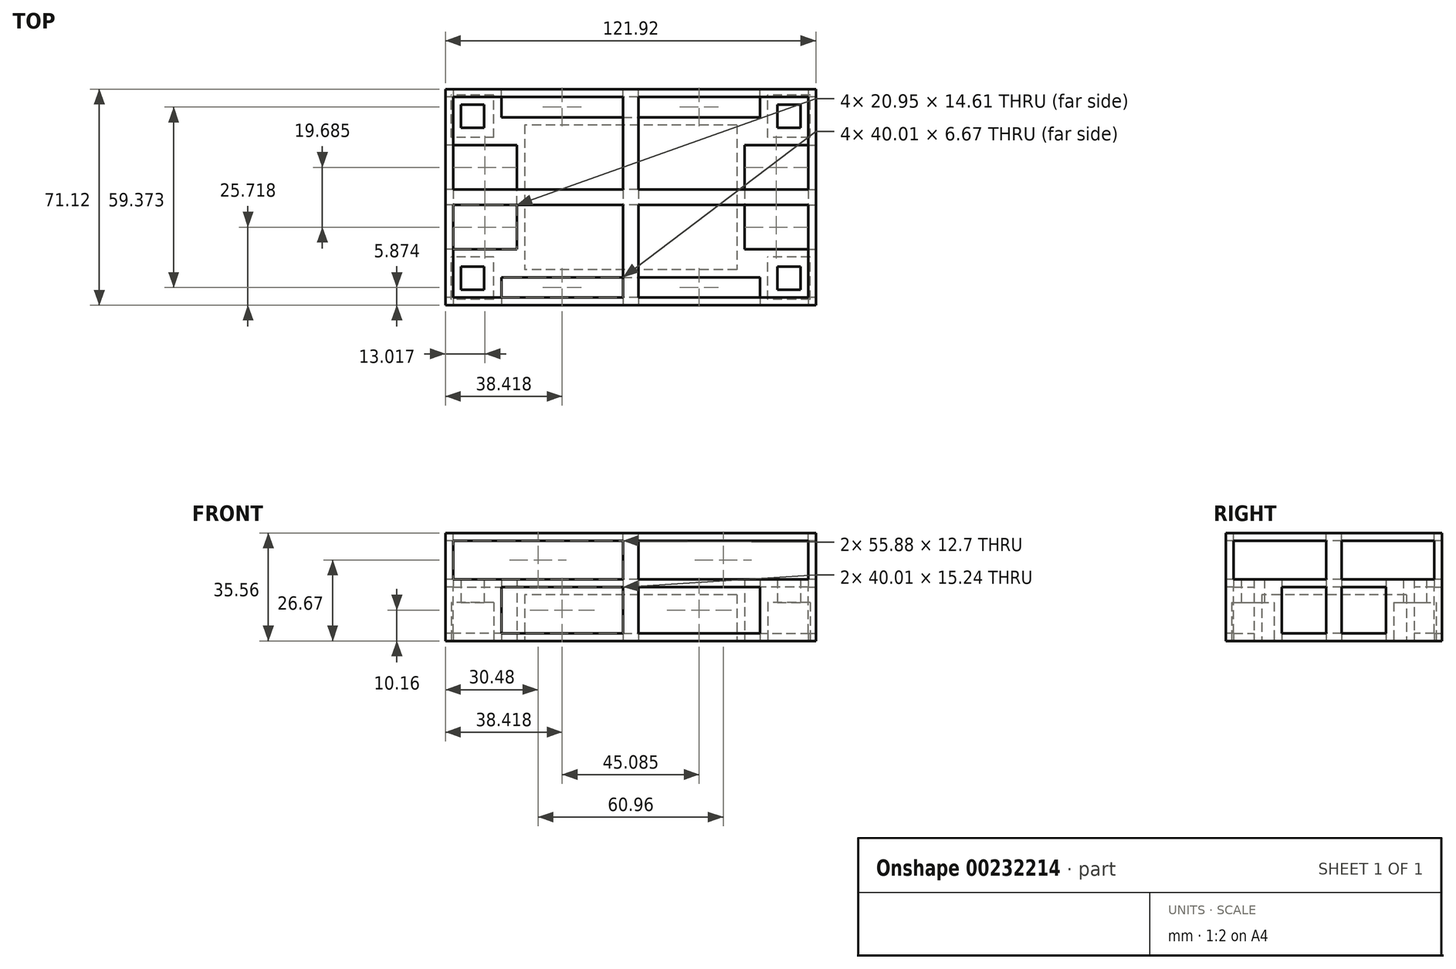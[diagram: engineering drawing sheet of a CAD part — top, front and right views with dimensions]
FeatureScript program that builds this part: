
annotation { "Feature Type Name" : "Feature", "Feature Type Description" : "" }
export const myFeature = defineFeature(function(context is Context, id is Id, definition is map)
    precondition{}
    {
        {
            var Q0;
            Q0=qCreatedBy(makeId("Top.planeOp"),FACE);
            var sketch = newSketch(context, id + "F0", { "sketchPlane" : qUnion([Q0])});
            skLineSegment(sketch, "E0.bottom", {"start": v(-60.96, 35.56) * mm, "end": v(60.96, 35.56) * mm});
            skLineSegment(sketch, "E0.top", {"start": v(-60.96, -35.56) * mm, "end": v(60.96, -35.56) * mm});
            skLineSegment(sketch, "E0.left", {"start": v(-60.96, 35.56) * mm, "end": v(-60.96, -35.56) * mm});
            skLineSegment(sketch, "E0.right", {"start": v(60.96, 35.56) * mm, "end": v(60.96, -35.56) * mm});
            skPoint(sketch, "E0.middle", {"position": v(0, 0) * mm});
            skSolve(sketch);
        }
        {
            var Q0;
            Q0=makeQuery(id+"F0.imprint","IMPRINT",FACE,{"disambiguationData":[TD([[makeQuery(id+"F0.imprint","IMPRINT",EDGE,{"derivedFrom":sQuery(id+"F0.wireOp",EDGE,"E0.bottom")}),-1.0]])]});
            extrude(context, id + "F1", {"entities" : qUnion([Q0]), "depth" : 35.56 * mm});
        }
        {
            var Q0;
            Q0=qCreatedBy(makeId("Top.planeOp"),FACE);
            var sketch = newSketch(context, id + "F2", { "sketchPlane" : qUnion([Q0])});
            skLineSegment(sketch, "E1.bottom", {"start": v(-52.07, 26.67) * mm, "end": v(52.07, 26.67) * mm});
            skLineSegment(sketch, "E1.top", {"start": v(-52.07, -26.67) * mm, "end": v(52.07, -26.67) * mm});
            skLineSegment(sketch, "E1.left", {"start": v(-52.07, 26.67) * mm, "end": v(-52.07, -26.67) * mm});
            skLineSegment(sketch, "E1.right", {"start": v(52.07, 26.67) * mm, "end": v(52.07, -26.67) * mm});
            skPoint(sketch, "E1.middle", {"position": v(0, 0) * mm});
            skLineSegment(sketch, "E2.bottom", {"start": v(-45.08, 19.68) * mm, "end": v(-59.05, 19.68) * mm});
            skLineSegment(sketch, "E2.top", {"start": v(-45.08, 33.66) * mm, "end": v(-59.05, 33.66) * mm});
            skLineSegment(sketch, "E2.left", {"start": v(-45.08, 19.68) * mm, "end": v(-45.08, 33.65) * mm});
            skLineSegment(sketch, "E2.right", {"start": v(-59.05, 19.68) * mm, "end": v(-59.05, 33.65) * mm});
            skPoint(sketch, "E2.middle", {"position": v(-52.07, 26.67) * mm});
            skLineSegment(sketch, "E3.bottom", {"start": v(-45.08, -33.65) * mm, "end": v(-59.05, -33.65) * mm});
            skLineSegment(sketch, "E3.top", {"start": v(-45.08, -19.68) * mm, "end": v(-59.05, -19.68) * mm});
            skLineSegment(sketch, "E3.left", {"start": v(-45.08, -33.65) * mm, "end": v(-45.08, -19.69) * mm});
            skLineSegment(sketch, "E3.right", {"start": v(-59.05, -33.65) * mm, "end": v(-59.05, -19.68) * mm});
            skPoint(sketch, "E3.middle", {"position": v(-52.07, -26.67) * mm});
            skLineSegment(sketch, "E4.bottom", {"start": v(59.05, -33.66) * mm, "end": v(45.08, -33.66) * mm});
            skLineSegment(sketch, "E4.top", {"start": v(59.05, -19.68) * mm, "end": v(45.08, -19.68) * mm});
            skLineSegment(sketch, "E4.left", {"start": v(59.05, -33.66) * mm, "end": v(59.05, -19.68) * mm});
            skLineSegment(sketch, "E4.right", {"start": v(45.08, -33.66) * mm, "end": v(45.08, -19.68) * mm});
            skPoint(sketch, "E4.middle", {"position": v(52.07, -26.67) * mm});
            skLineSegment(sketch, "E5.bottom", {"start": v(59.06, 19.69) * mm, "end": v(45.09, 19.69) * mm});
            skLineSegment(sketch, "E5.top", {"start": v(59.06, 33.66) * mm, "end": v(45.09, 33.66) * mm});
            skLineSegment(sketch, "E5.left", {"start": v(59.06, 19.69) * mm, "end": v(59.06, 33.66) * mm});
            skLineSegment(sketch, "E5.right", {"start": v(45.09, 19.69) * mm, "end": v(45.09, 33.66) * mm});
            skPoint(sketch, "E5.middle", {"position": v(52.07, 26.67) * mm});
            skLineSegment(sketch, "E6.bottom", {"start": v(-48.26, -22.86) * mm, "end": v(-55.88, -22.86) * mm});
            skLineSegment(sketch, "E6.top", {"start": v(-48.26, -30.48) * mm, "end": v(-55.88, -30.48) * mm});
            skLineSegment(sketch, "E6.left", {"start": v(-48.26, -22.86) * mm, "end": v(-48.26, -30.48) * mm});
            skLineSegment(sketch, "E6.right", {"start": v(-55.88, -22.86) * mm, "end": v(-55.88, -30.48) * mm});
            skLineSegment(sketch, "E7.bottom", {"start": v(-48.26, 30.48) * mm, "end": v(-55.88, 30.48) * mm});
            skLineSegment(sketch, "E7.top", {"start": v(-48.26, 22.86) * mm, "end": v(-55.88, 22.86) * mm});
            skLineSegment(sketch, "E7.left", {"start": v(-48.26, 30.48) * mm, "end": v(-48.26, 22.86) * mm});
            skLineSegment(sketch, "E7.right", {"start": v(-55.88, 30.48) * mm, "end": v(-55.88, 22.86) * mm});
            skLineSegment(sketch, "E8.bottom", {"start": v(55.88, -22.86) * mm, "end": v(48.26, -22.86) * mm});
            skLineSegment(sketch, "E8.top", {"start": v(55.88, -30.48) * mm, "end": v(48.26, -30.48) * mm});
            skLineSegment(sketch, "E8.left", {"start": v(55.88, -22.86) * mm, "end": v(55.88, -30.48) * mm});
            skLineSegment(sketch, "E8.right", {"start": v(48.26, -22.86) * mm, "end": v(48.26, -30.48) * mm});
            skLineSegment(sketch, "E9.bottom", {"start": v(55.88, 30.48) * mm, "end": v(48.26, 30.48) * mm});
            skLineSegment(sketch, "E9.top", {"start": v(55.88, 22.86) * mm, "end": v(48.26, 22.86) * mm});
            skLineSegment(sketch, "E9.left", {"start": v(55.88, 30.48) * mm, "end": v(55.88, 22.86) * mm});
            skLineSegment(sketch, "E9.right", {"start": v(48.26, 30.48) * mm, "end": v(48.26, 22.86) * mm});
            skSolve(sketch);
        }
        {
            var Q0;
            {var subQ4=sQuery(id+"F2.wireOp",EDGE,"E4.bottom");Q0=makeQuery(id+"F2.imprint","IMPRINT",FACE,{"disambiguationData":[TD([[makeQuery(id+"F2.imprint","IMPRINT",EDGE,{"derivedFrom":subQ4}),-1.0]])]});}
            var Q1;
            {var subQ0=sQuery(id+"F2.wireOp",EDGE,"E4.right");var subQ3=sQuery(id+"F2.wireOp",EDGE,"E1.top");var subQ4=makeQuery(id+"F2.imprint","INTERSECT",VERTEX,{"derivedFrom":[subQ3,subQ0]});Q1=makeQuery(id+"F2.imprint","IMPRINT",FACE,{"disambiguationData":[TD([[makeQuery(id+"F2.imprint","IMPRINT",EDGE,{"disambiguationData":[TD([[subQ4,-1.0]])],"derivedFrom":subQ3}),1.0]])]});}
            var Q2;
            {var subQ0=sQuery(id+"F2.wireOp",EDGE,"E1.right");var subQ1=sQuery(id+"F2.wireOp",EDGE,"E1.top");var subQ2=makeQuery(id+"F2.imprint","INTERSECT",VERTEX,{"derivedFrom":[subQ1,subQ0]});Q2=makeQuery(id+"F2.imprint","IMPRINT",FACE,{"disambiguationData":[TD([[makeQuery(id+"F2.imprint","IMPRINT",EDGE,{"disambiguationData":[TD([[subQ2,1.0]])],"derivedFrom":subQ1}),1.0]])]});}
            var Q3;
            {var subQ0=sQuery(id+"F2.wireOp",EDGE,"E8.top");Q3=makeQuery(id+"F2.imprint","IMPRINT",FACE,{"disambiguationData":[TD([[makeQuery(id+"F2.imprint","IMPRINT",EDGE,{"derivedFrom":subQ0}),-1.0]])]});}
            var Q4;
            {var subQ4=sQuery(id+"F2.wireOp",EDGE,"E5.top");Q4=makeQuery(id+"F2.imprint","IMPRINT",FACE,{"disambiguationData":[TD([[makeQuery(id+"F2.imprint","IMPRINT",EDGE,{"derivedFrom":subQ4}),1.0]])]});}
            var Q5;
            {var subQ0=sQuery(id+"F2.wireOp",EDGE,"E5.right");var subQ3=sQuery(id+"F2.wireOp",EDGE,"E1.bottom");var subQ4=makeQuery(id+"F2.imprint","INTERSECT",VERTEX,{"derivedFrom":[subQ3,subQ0]});Q5=makeQuery(id+"F2.imprint","IMPRINT",FACE,{"disambiguationData":[TD([[makeQuery(id+"F2.imprint","IMPRINT",EDGE,{"disambiguationData":[TD([[subQ4,-1.0]])],"derivedFrom":subQ3}),-1.0]])]});}
            var Q6;
            {var subQ4=sQuery(id+"F2.wireOp",EDGE,"E9.bottom");Q6=makeQuery(id+"F2.imprint","IMPRINT",FACE,{"disambiguationData":[TD([[makeQuery(id+"F2.imprint","IMPRINT",EDGE,{"derivedFrom":subQ4}),1.0]])]});}
            var Q7;
            {var subQ0=sQuery(id+"F2.wireOp",EDGE,"E1.right");var subQ1=sQuery(id+"F2.wireOp",EDGE,"E1.bottom");var subQ2=makeQuery(id+"F2.imprint","INTERSECT",VERTEX,{"derivedFrom":[subQ1,subQ0]});Q7=makeQuery(id+"F2.imprint","IMPRINT",FACE,{"disambiguationData":[TD([[makeQuery(id+"F2.imprint","IMPRINT",EDGE,{"disambiguationData":[TD([[subQ2,1.0]])],"derivedFrom":subQ1}),-1.0]])]});}
            var Q8;
            {var subQ0=sQuery(id+"F2.wireOp",EDGE,"E2.left");var subQ3=sQuery(id+"F2.wireOp",EDGE,"E1.bottom");var subQ4=makeQuery(id+"F2.imprint","INTERSECT",VERTEX,{"derivedFrom":[subQ3,subQ0]});Q8=makeQuery(id+"F2.imprint","IMPRINT",FACE,{"disambiguationData":[TD([[makeQuery(id+"F2.imprint","IMPRINT",EDGE,{"disambiguationData":[TD([[subQ4,1.0]])],"derivedFrom":subQ3}),-1.0]])]});}
            var Q9;
            {var subQ8=sQuery(id+"F2.wireOp",EDGE,"E7.bottom");Q9=makeQuery(id+"F2.imprint","IMPRINT",FACE,{"disambiguationData":[TD([[makeQuery(id+"F2.imprint","IMPRINT",EDGE,{"derivedFrom":subQ8}),1.0]])]});}
            var Q10;
            {var subQ0=sQuery(id+"F2.wireOp",EDGE,"E2.top");Q10=makeQuery(id+"F2.imprint","IMPRINT",FACE,{"disambiguationData":[TD([[makeQuery(id+"F2.imprint","IMPRINT",EDGE,{"derivedFrom":subQ0}),1.0]])]});}
            var Q11;
            {var subQ0=sQuery(id+"F2.wireOp",EDGE,"E1.left");var subQ1=sQuery(id+"F2.wireOp",EDGE,"E1.bottom");var subQ2=makeQuery(id+"F2.imprint","INTERSECT",VERTEX,{"derivedFrom":[subQ1,subQ0]});Q11=makeQuery(id+"F2.imprint","IMPRINT",FACE,{"disambiguationData":[TD([[makeQuery(id+"F2.imprint","IMPRINT",EDGE,{"disambiguationData":[TD([[subQ2,-1.0]])],"derivedFrom":subQ1}),-1.0]])]});}
            var Q12;
            {var subQ0=sQuery(id+"F2.wireOp",EDGE,"E3.bottom");Q12=makeQuery(id+"F2.imprint","IMPRINT",FACE,{"disambiguationData":[TD([[makeQuery(id+"F2.imprint","IMPRINT",EDGE,{"derivedFrom":subQ0}),-1.0]])]});}
            var Q13;
            {var subQ0=sQuery(id+"F2.wireOp",EDGE,"E6.top");Q13=makeQuery(id+"F2.imprint","IMPRINT",FACE,{"disambiguationData":[TD([[makeQuery(id+"F2.imprint","IMPRINT",EDGE,{"derivedFrom":subQ0}),-1.0]])]});}
            var Q14;
            {var subQ0=sQuery(id+"F2.wireOp",EDGE,"E1.left");var subQ1=sQuery(id+"F2.wireOp",EDGE,"E1.top");var subQ2=makeQuery(id+"F2.imprint","INTERSECT",VERTEX,{"derivedFrom":[subQ1,subQ0]});Q14=makeQuery(id+"F2.imprint","IMPRINT",FACE,{"disambiguationData":[TD([[makeQuery(id+"F2.imprint","IMPRINT",EDGE,{"disambiguationData":[TD([[subQ2,-1.0]])],"derivedFrom":subQ1}),1.0]])]});}
            var Q15;
            {var subQ0=sQuery(id+"F2.wireOp",EDGE,"E3.left");var subQ5=sQuery(id+"F2.wireOp",EDGE,"E1.top");var subQ6=makeQuery(id+"F2.imprint","INTERSECT",VERTEX,{"derivedFrom":[subQ5,subQ0]});Q15=makeQuery(id+"F2.imprint","IMPRINT",FACE,{"disambiguationData":[TD([[makeQuery(id+"F2.imprint","IMPRINT",EDGE,{"disambiguationData":[TD([[subQ6,1.0]])],"derivedFrom":subQ5}),1.0]])]});}
            extrude(context, id + "F3", {"entities" : qUnion([Q0, Q1, Q2, Q3, Q4, Q5, Q6, Q7, Q8, Q9, Q10, Q11, Q12, Q13, Q14, Q15]), "operationType" : NewBodyOperationType.REMOVE, "depth" : 12.7 * mm});
        }
        {
            var Q0;
            Q0=makeQuery(id+"F1.opExtrude","CAP_FACE",FACE,{"disambiguationData":[OSD([sQuery(id+"F0.wireOp",EDGE,"E0.bottom"),sQuery(id+"F0.wireOp",EDGE,"E0.top"),sQuery(id+"F0.wireOp",EDGE,"E0.left"),sQuery(id+"F0.wireOp",EDGE,"E0.right")])],"isStart":true});
            var sketch = newSketch(context, id + "F4", { "sketchPlane" : qUnion([Q0])});
            skLineSegment(sketch, "E10.bottom", {"start": v(34.93, -23.81) * mm, "end": v(-34.93, -23.81) * mm});
            skLineSegment(sketch, "E10.top", {"start": v(34.92, 23.81) * mm, "end": v(-34.93, 23.81) * mm});
            skLineSegment(sketch, "E10.left", {"start": v(34.93, -23.81) * mm, "end": v(34.92, 23.81) * mm});
            skLineSegment(sketch, "E10.right", {"start": v(-34.92, -23.81) * mm, "end": v(-34.93, 23.81) * mm});
            skPoint(sketch, "E10.middle", {"position": v(0, 0) * mm});
            skSolve(sketch);
        }
        {
            var Q0;
            Q0=makeQuery(id+"F4.imprint","IMPRINT",FACE,{"disambiguationData":[TD([[makeQuery(id+"F4.imprint","IMPRINT",EDGE,{"derivedFrom":sQuery(id+"F4.wireOp",EDGE,"E10.bottom")}),-1.0]])]});
            extrude(context, id + "F5", {"entities" : qUnion([Q0]), "operationType" : NewBodyOperationType.REMOVE, "oppositeDirection" : true, "depth" : 15.24 * mm});
        }
        {
            var Q0;
            Q0=makeQuery(id+"F1.opExtrude","SWEPT_FACE",FACE,{"disambiguationData":[OSD([sQuery(id+"F0.wireOp",EDGE,"E0.top")])]});
            var sketch = newSketch(context, id + "F6", { "sketchPlane" : qUnion([Q0])});
            skLineSegment(sketch, "E11", {"start": v(0, 0) * mm, "end": v(0, 35.56) * mm});
            skLineSegment(sketch, "E12.bottom", {"start": v(-60.96, 0) * mm, "end": v(60.96, 0) * mm});
            skLineSegment(sketch, "E12.top", {"start": v(-60.96, 17.78) * mm, "end": v(60.96, 17.78) * mm});
            skLineSegment(sketch, "E12.left", {"start": v(-60.96, 0) * mm, "end": v(-60.96, 17.78) * mm});
            skLineSegment(sketch, "E12.right", {"start": v(60.96, 0) * mm, "end": v(60.96, 17.78) * mm});
            skLineSegment(sketch, "E13.bottom", {"start": v(-60.96, 35.56) * mm, "end": v(60.96, 35.56) * mm});
            skLineSegment(sketch, "E13.left", {"start": v(-60.96, 35.56) * mm, "end": v(-60.96, 17.78) * mm});
            skLineSegment(sketch, "E13.right", {"start": v(60.96, 35.56) * mm, "end": v(60.96, 17.78) * mm});
            skLineSegment(sketch, "E14", {"start": v(-60.96, 35.56) * mm, "end": v(0, 35.56) * mm});
            skLineSegment(sketch, "E15", {"start": v(0, 35.56) * mm, "end": v(60.96, 35.56) * mm});
            skLineSegment(sketch, "E16", {"start": v(-30.48, 35.56) * mm, "end": v(-30.48, 17.78) * mm});
            skLineSegment(sketch, "E17", {"start": v(30.48, 35.56) * mm, "end": v(30.48, 17.78) * mm});
            skLineSegment(sketch, "E18", {"start": v(-60.96, 17.78) * mm, "end": v(-60.96, 35.56) * mm});
            skLineSegment(sketch, "E19", {"start": v(60.96, 17.78) * mm, "end": v(60.96, 35.56) * mm});
            skLineSegment(sketch, "E20", {"start": v(-60.96, 26.67) * mm, "end": v(0, 26.67) * mm});
            skLineSegment(sketch, "E21", {"start": v(0, 26.67) * mm, "end": v(60.96, 26.67) * mm});
            skLineSegment(sketch, "E22.bottom", {"start": v(-2.54, 33.02) * mm, "end": v(-58.42, 33.02) * mm});
            skLineSegment(sketch, "E22.top", {"start": v(-2.54, 20.32) * mm, "end": v(-58.42, 20.32) * mm});
            skLineSegment(sketch, "E22.left", {"start": v(-2.54, 33.02) * mm, "end": v(-2.54, 20.32) * mm});
            skLineSegment(sketch, "E22.right", {"start": v(-58.42, 33.02) * mm, "end": v(-58.42, 20.32) * mm});
            skPoint(sketch, "E22.middle", {"position": v(-30.48, 26.67) * mm});
            skLineSegment(sketch, "E23.bottom", {"start": v(58.42, 33.02) * mm, "end": v(2.54, 33.02) * mm});
            skLineSegment(sketch, "E23.top", {"start": v(58.42, 20.32) * mm, "end": v(2.54, 20.32) * mm});
            skLineSegment(sketch, "E23.left", {"start": v(58.42, 33.02) * mm, "end": v(58.42, 20.32) * mm});
            skLineSegment(sketch, "E23.right", {"start": v(2.54, 33.02) * mm, "end": v(2.54, 20.32) * mm});
            skPoint(sketch, "E23.middle", {"position": v(30.48, 26.67) * mm});
            skSolve(sketch);
        }
        {
            var Q0;
            {var subQ0=sQuery(id+"F6.wireOp",EDGE,"E22.bottom");var subQ1=sQuery(id+"F6.wireOp",EDGE,"E16");var subQ2=makeQuery(id+"F6.imprint","INTERSECT",VERTEX,{"derivedFrom":[subQ1,subQ0]});Q0=makeQuery(id+"F6.imprint","IMPRINT",FACE,{"disambiguationData":[TD([[makeQuery(id+"F6.imprint","IMPRINT",EDGE,{"disambiguationData":[TD([[subQ2,-1.0]])],"derivedFrom":subQ1}),-1.0]])]});}
            var Q1;
            {var subQ0=sQuery(id+"F6.wireOp",EDGE,"E22.bottom");var subQ1=sQuery(id+"F6.wireOp",EDGE,"E16");var subQ2=makeQuery(id+"F6.imprint","INTERSECT",VERTEX,{"derivedFrom":[subQ1,subQ0]});Q1=makeQuery(id+"F6.imprint","IMPRINT",FACE,{"disambiguationData":[TD([[makeQuery(id+"F6.imprint","IMPRINT",EDGE,{"disambiguationData":[TD([[subQ2,-1.0]])],"derivedFrom":subQ1}),1.0]])]});}
            var Q2;
            {var subQ0=sQuery(id+"F6.wireOp",EDGE,"E20");var subQ1=sQuery(id+"F6.wireOp",EDGE,"E16");var subQ2=makeQuery(id+"F6.imprint","INTERSECT",VERTEX,{"derivedFrom":[subQ1,subQ0]});Q2=makeQuery(id+"F6.imprint","IMPRINT",FACE,{"disambiguationData":[TD([[makeQuery(id+"F6.imprint","IMPRINT",EDGE,{"disambiguationData":[TD([[subQ2,-1.0]])],"derivedFrom":subQ1}),1.0]])]});}
            var Q3;
            {var subQ0=sQuery(id+"F6.wireOp",EDGE,"E20");var subQ1=sQuery(id+"F6.wireOp",EDGE,"E16");var subQ2=makeQuery(id+"F6.imprint","INTERSECT",VERTEX,{"derivedFrom":[subQ1,subQ0]});Q3=makeQuery(id+"F6.imprint","IMPRINT",FACE,{"disambiguationData":[TD([[makeQuery(id+"F6.imprint","IMPRINT",EDGE,{"disambiguationData":[TD([[subQ2,-1.0]])],"derivedFrom":subQ1}),-1.0]])]});}
            var Q4;
            {var subQ0=sQuery(id+"F6.wireOp",EDGE,"E23.bottom");var subQ1=sQuery(id+"F6.wireOp",EDGE,"E17");var subQ2=makeQuery(id+"F6.imprint","INTERSECT",VERTEX,{"derivedFrom":[subQ1,subQ0]});Q4=makeQuery(id+"F6.imprint","IMPRINT",FACE,{"disambiguationData":[TD([[makeQuery(id+"F6.imprint","IMPRINT",EDGE,{"disambiguationData":[TD([[subQ2,-1.0]])],"derivedFrom":subQ1}),-1.0]])]});}
            var Q5;
            {var subQ0=sQuery(id+"F6.wireOp",EDGE,"E21");var subQ1=sQuery(id+"F6.wireOp",EDGE,"E17");var subQ2=makeQuery(id+"F6.imprint","INTERSECT",VERTEX,{"derivedFrom":[subQ1,subQ0]});Q5=makeQuery(id+"F6.imprint","IMPRINT",FACE,{"disambiguationData":[TD([[makeQuery(id+"F6.imprint","IMPRINT",EDGE,{"disambiguationData":[TD([[subQ2,-1.0]])],"derivedFrom":subQ1}),-1.0]])]});}
            var Q6;
            {var subQ0=sQuery(id+"F6.wireOp",EDGE,"E23.bottom");var subQ1=sQuery(id+"F6.wireOp",EDGE,"E17");var subQ2=makeQuery(id+"F6.imprint","INTERSECT",VERTEX,{"derivedFrom":[subQ1,subQ0]});Q6=makeQuery(id+"F6.imprint","IMPRINT",FACE,{"disambiguationData":[TD([[makeQuery(id+"F6.imprint","IMPRINT",EDGE,{"disambiguationData":[TD([[subQ2,-1.0]])],"derivedFrom":subQ1}),1.0]])]});}
            var Q7;
            {var subQ0=sQuery(id+"F6.wireOp",EDGE,"E21");var subQ1=sQuery(id+"F6.wireOp",EDGE,"E17");var subQ2=makeQuery(id+"F6.imprint","INTERSECT",VERTEX,{"derivedFrom":[subQ1,subQ0]});Q7=makeQuery(id+"F6.imprint","IMPRINT",FACE,{"disambiguationData":[TD([[makeQuery(id+"F6.imprint","IMPRINT",EDGE,{"disambiguationData":[TD([[subQ2,-1.0]])],"derivedFrom":subQ1}),1.0]])]});}
            var Q8;
            Q8=makeQuery(id+"F1.opExtrude","SWEPT_FACE",FACE,{"disambiguationData":[OSD([sQuery(id+"F0.wireOp",EDGE,"E0.bottom")])]});
            extrude(context, id + "F7", {"entities" : qUnion([Q0, Q1, Q2, Q3, Q4, Q5, Q6, Q7]), "operationType" : NewBodyOperationType.REMOVE, "endBound" : BoundingType.UP_TO_SURFACE, "oppositeDirection" : true, "endBoundEntityFace" : qUnion([Q8]), "depth" : 25.4 * mm});
        }
        {
            var Q0;
            Q0=makeQuery(id+"F1.opExtrude","SWEPT_FACE",FACE,{"disambiguationData":[OSD([sQuery(id+"F0.wireOp",EDGE,"E0.left")])]});
            var sketch = newSketch(context, id + "F8", { "sketchPlane" : qUnion([Q0])});
            skLineSegment(sketch, "E24.bottom", {"start": v(-35.56, 0) * mm, "end": v(35.56, 0) * mm});
            skLineSegment(sketch, "E24.top", {"start": v(-35.56, 35.56) * mm, "end": v(35.56, 35.56) * mm});
            skLineSegment(sketch, "E24.left", {"start": v(-35.56, 0) * mm, "end": v(-35.56, 35.56) * mm});
            skLineSegment(sketch, "E24.right", {"start": v(35.56, 0) * mm, "end": v(35.56, 35.56) * mm});
            skLineSegment(sketch, "E25.top", {"start": v(-35.56, 17.78) * mm, "end": v(35.56, 17.78) * mm});
            skLineSegment(sketch, "E25.left", {"start": v(-35.56, 0) * mm, "end": v(-35.56, 17.78) * mm});
            skLineSegment(sketch, "E25.right", {"start": v(35.56, 0) * mm, "end": v(35.56, 17.78) * mm});
            skLineSegment(sketch, "E26.left", {"start": v(-35.56, 35.56) * mm, "end": v(-35.56, 17.78) * mm});
            skLineSegment(sketch, "E26.right", {"start": v(35.56, 35.56) * mm, "end": v(35.56, 17.78) * mm});
            skLineSegment(sketch, "E27", {"start": v(0, 0) * mm, "end": v(0, 35.56) * mm});
            skLineSegment(sketch, "E28", {"start": v(0, 35.56) * mm, "end": v(-35.56, 35.56) * mm});
            skLineSegment(sketch, "E29", {"start": v(-17.78, 35.56) * mm, "end": v(-17.78, 17.78) * mm});
            skLineSegment(sketch, "E30", {"start": v(-35.56, 26.67) * mm, "end": v(0, 26.67) * mm});
            skLineSegment(sketch, "E31", {"start": v(0, 26.67) * mm, "end": v(35.56, 26.67) * mm});
            skLineSegment(sketch, "E32", {"start": v(17.78, 35.56) * mm, "end": v(17.78, 17.78) * mm});
            skPoint(sketch, "E32.startSnap0", {"position": v(17.78, 26.67) * mm});
            skPoint(sketch, "E32.endSnap0", {"position": v(0, 17.78) * mm});
            skPoint(sketch, "E33", {"position": v(-17.78, 26.67) * mm});
            skLineSegment(sketch, "E34.bottom", {"start": v(-33.02, 33.02) * mm, "end": v(-2.54, 33.02) * mm});
            skLineSegment(sketch, "E34.top", {"start": v(-33.02, 20.32) * mm, "end": v(-2.54, 20.32) * mm});
            skLineSegment(sketch, "E34.left", {"start": v(-33.02, 33.02) * mm, "end": v(-33.02, 20.32) * mm});
            skLineSegment(sketch, "E34.right", {"start": v(-2.54, 33.02) * mm, "end": v(-2.54, 20.32) * mm});
            skLineSegment(sketch, "E35.bottom", {"start": v(2.54, 33.02) * mm, "end": v(33.02, 33.02) * mm});
            skLineSegment(sketch, "E35.top", {"start": v(2.54, 20.32) * mm, "end": v(33.02, 20.32) * mm});
            skLineSegment(sketch, "E35.left", {"start": v(2.54, 33.02) * mm, "end": v(2.54, 20.32) * mm});
            skLineSegment(sketch, "E35.right", {"start": v(33.02, 33.02) * mm, "end": v(33.02, 20.32) * mm});
            skSolve(sketch);
        }
        {
            var Q0;
            {var subQ0=sQuery(id+"F8.wireOp",EDGE,"E34.bottom");var subQ1=sQuery(id+"F8.wireOp",EDGE,"E29");var subQ2=makeQuery(id+"F8.imprint","INTERSECT",VERTEX,{"derivedFrom":[subQ1,subQ0]});Q0=makeQuery(id+"F8.imprint","IMPRINT",FACE,{"disambiguationData":[TD([[makeQuery(id+"F8.imprint","IMPRINT",EDGE,{"disambiguationData":[TD([[subQ2,-1.0]])],"derivedFrom":subQ1}),-1.0]])]});}
            var Q1;
            {var subQ0=sQuery(id+"F8.wireOp",EDGE,"E34.bottom");var subQ1=sQuery(id+"F8.wireOp",EDGE,"E29");var subQ2=makeQuery(id+"F8.imprint","INTERSECT",VERTEX,{"derivedFrom":[subQ1,subQ0]});Q1=makeQuery(id+"F8.imprint","IMPRINT",FACE,{"disambiguationData":[TD([[makeQuery(id+"F8.imprint","IMPRINT",EDGE,{"disambiguationData":[TD([[subQ2,-1.0]])],"derivedFrom":subQ1}),1.0]])]});}
            var Q2;
            {var subQ0=sQuery(id+"F8.wireOp",EDGE,"E30");var subQ1=sQuery(id+"F8.wireOp",EDGE,"E29");var subQ2=makeQuery(id+"F8.imprint","INTERSECT",VERTEX,{"derivedFrom":[subQ1,subQ0]});Q2=makeQuery(id+"F8.imprint","IMPRINT",FACE,{"disambiguationData":[TD([[makeQuery(id+"F8.imprint","IMPRINT",EDGE,{"disambiguationData":[TD([[subQ2,-1.0]])],"derivedFrom":subQ1}),1.0]])]});}
            var Q3;
            {var subQ0=sQuery(id+"F8.wireOp",EDGE,"E30");var subQ1=sQuery(id+"F8.wireOp",EDGE,"E29");var subQ2=makeQuery(id+"F8.imprint","INTERSECT",VERTEX,{"derivedFrom":[subQ1,subQ0]});Q3=makeQuery(id+"F8.imprint","IMPRINT",FACE,{"disambiguationData":[TD([[makeQuery(id+"F8.imprint","IMPRINT",EDGE,{"disambiguationData":[TD([[subQ2,-1.0]])],"derivedFrom":subQ1}),-1.0]])]});}
            var Q4;
            {var subQ0=sQuery(id+"F8.wireOp",EDGE,"E35.left");var subQ1=sQuery(id+"F8.wireOp",EDGE,"E31");var subQ2=makeQuery(id+"F8.imprint","INTERSECT",VERTEX,{"derivedFrom":[subQ1,subQ0]});Q4=makeQuery(id+"F8.imprint","IMPRINT",FACE,{"disambiguationData":[TD([[makeQuery(id+"F8.imprint","IMPRINT",EDGE,{"disambiguationData":[TD([[subQ2,-1.0]])],"derivedFrom":subQ1}),-1.0]])]});}
            var Q5;
            {var subQ0=sQuery(id+"F8.wireOp",EDGE,"E35.left");var subQ1=sQuery(id+"F8.wireOp",EDGE,"E31");var subQ2=makeQuery(id+"F8.imprint","INTERSECT",VERTEX,{"derivedFrom":[subQ1,subQ0]});Q5=makeQuery(id+"F8.imprint","IMPRINT",FACE,{"disambiguationData":[TD([[makeQuery(id+"F8.imprint","IMPRINT",EDGE,{"disambiguationData":[TD([[subQ2,-1.0]])],"derivedFrom":subQ1}),1.0]])]});}
            var Q6;
            {var subQ0=sQuery(id+"F8.wireOp",EDGE,"E32");var subQ1=sQuery(id+"F8.wireOp",EDGE,"E31");var subQ2=makeQuery(id+"F8.imprint","INTERSECT",VERTEX,{"derivedFrom":[subQ1,subQ0]});Q6=makeQuery(id+"F8.imprint","IMPRINT",FACE,{"disambiguationData":[TD([[makeQuery(id+"F8.imprint","IMPRINT",EDGE,{"disambiguationData":[TD([[subQ2,-1.0]])],"derivedFrom":subQ1}),1.0]])]});}
            var Q7;
            {var subQ0=sQuery(id+"F8.wireOp",EDGE,"E32");var subQ1=sQuery(id+"F8.wireOp",EDGE,"E31");var subQ2=makeQuery(id+"F8.imprint","INTERSECT",VERTEX,{"derivedFrom":[subQ1,subQ0]});Q7=makeQuery(id+"F8.imprint","IMPRINT",FACE,{"disambiguationData":[TD([[makeQuery(id+"F8.imprint","IMPRINT",EDGE,{"disambiguationData":[TD([[subQ2,-1.0]])],"derivedFrom":subQ1}),-1.0]])]});}
            var Q8;
            Q8=makeQuery(id+"F1.opExtrude","SWEPT_FACE",FACE,{"disambiguationData":[OSD([sQuery(id+"F0.wireOp",EDGE,"E0.right")])]});
            extrude(context, id + "F9", {"entities" : qUnion([Q0, Q1, Q2, Q3, Q4, Q5, Q6, Q7]), "operationType" : NewBodyOperationType.REMOVE, "endBound" : BoundingType.UP_TO_SURFACE, "oppositeDirection" : true, "endBoundEntityFace" : qUnion([Q8]), "depth" : 25.4 * mm});
        }
        {
            var Q0;
            Q0=makeQuery(id+"F1.opExtrude","CAP_FACE",FACE,{"disambiguationData":[OSD([sQuery(id+"F0.wireOp",EDGE,"E0.bottom"),sQuery(id+"F0.wireOp",EDGE,"E0.top"),sQuery(id+"F0.wireOp",EDGE,"E0.left"),sQuery(id+"F0.wireOp",EDGE,"E0.right")])],"isStart":false});
            var sketch = newSketch(context, id + "F10", { "sketchPlane" : qUnion([Q0])});
            skLineSegment(sketch, "E36.bottom", {"start": v(-60.96, 35.56) * mm, "end": v(60.96, 35.56) * mm});
            skLineSegment(sketch, "E36.top", {"start": v(-60.96, -35.56) * mm, "end": v(60.96, -35.56) * mm});
            skLineSegment(sketch, "E36.left", {"start": v(-60.96, 35.56) * mm, "end": v(-60.96, -35.56) * mm});
            skLineSegment(sketch, "E36.right", {"start": v(60.96, 35.56) * mm, "end": v(60.96, -35.56) * mm});
            skLineSegment(sketch, "E37.bottom", {"start": v(-60.96, 0) * mm, "end": v(0, 0) * mm});
            skLineSegment(sketch, "E37.top", {"start": v(-60.96, -35.56) * mm, "end": v(0, -35.56) * mm});
            skLineSegment(sketch, "E37.left", {"start": v(-60.96, 0) * mm, "end": v(-60.96, -35.56) * mm});
            skLineSegment(sketch, "E37.right", {"start": v(0, 0) * mm, "end": v(0, -35.56) * mm});
            skLineSegment(sketch, "E38.bottom", {"start": v(0, 0) * mm, "end": v(60.96, 0) * mm});
            skLineSegment(sketch, "E38.top", {"start": v(0, 35.56) * mm, "end": v(60.96, 35.56) * mm});
            skLineSegment(sketch, "E38.left", {"start": v(0, 0) * mm, "end": v(0, 35.56) * mm});
            skLineSegment(sketch, "E38.right", {"start": v(60.96, 0) * mm, "end": v(60.96, 35.56) * mm});
            skLineSegment(sketch, "E39.bottom", {"start": v(-60.96, 35.56) * mm, "end": v(0, 35.56) * mm});
            skLineSegment(sketch, "E39.left", {"start": v(-60.96, 35.56) * mm, "end": v(-60.96, 0) * mm});
            skLineSegment(sketch, "E39.right", {"start": v(0, 35.56) * mm, "end": v(0, 0) * mm});
            skLineSegment(sketch, "E40.top", {"start": v(0, -35.56) * mm, "end": v(60.96, -35.56) * mm});
            skLineSegment(sketch, "E40.right", {"start": v(60.96, 0) * mm, "end": v(60.96, -35.56) * mm});
            skLineSegment(sketch, "E41", {"start": v(-30.48, 0) * mm, "end": v(-30.48, 35.56) * mm});
            skLineSegment(sketch, "E42", {"start": v(-60.96, 17.78) * mm, "end": v(0, 17.78) * mm});
            skLineSegment(sketch, "E43", {"start": v(0, 17.78) * mm, "end": v(60.96, 17.78) * mm});
            skLineSegment(sketch, "E44", {"start": v(30.48, 35.56) * mm, "end": v(30.48, 0) * mm});
            skLineSegment(sketch, "E45", {"start": v(30.48, 0) * mm, "end": v(30.48, -35.56) * mm});
            skLineSegment(sketch, "E46", {"start": v(-30.48, -35.56) * mm, "end": v(-30.48, 0) * mm});
            skLineSegment(sketch, "E47", {"start": v(-60.96, -17.78) * mm, "end": v(0, -17.78) * mm});
            skLineSegment(sketch, "E48", {"start": v(0, -17.78) * mm, "end": v(60.96, -17.78) * mm});
            skPoint(sketch, "E49", {"position": v(-30.48, 17.78) * mm});
            skPoint(sketch, "E50", {"position": v(30.48, 17.78) * mm});
            skPoint(sketch, "E51", {"position": v(-30.48, -17.78) * mm});
            skPoint(sketch, "E52", {"position": v(30.48, -17.78) * mm});
            skLineSegment(sketch, "E53.bottom", {"start": v(-2.54, 33.02) * mm, "end": v(-58.42, 33.02) * mm});
            skLineSegment(sketch, "E53.top", {"start": v(-2.54, 2.54) * mm, "end": v(-58.42, 2.54) * mm});
            skLineSegment(sketch, "E53.left", {"start": v(-2.54, 33.02) * mm, "end": v(-2.54, 2.54) * mm});
            skLineSegment(sketch, "E53.right", {"start": v(-58.42, 33.02) * mm, "end": v(-58.42, 2.54) * mm});
            skLineSegment(sketch, "E54.bottom", {"start": v(58.42, 33.02) * mm, "end": v(2.54, 33.02) * mm});
            skLineSegment(sketch, "E54.top", {"start": v(58.42, 2.54) * mm, "end": v(2.54, 2.54) * mm});
            skLineSegment(sketch, "E54.left", {"start": v(58.42, 33.02) * mm, "end": v(58.42, 2.54) * mm});
            skLineSegment(sketch, "E54.right", {"start": v(2.54, 33.02) * mm, "end": v(2.54, 2.54) * mm});
            skLineSegment(sketch, "E55.bottom", {"start": v(-2.54, -2.54) * mm, "end": v(-58.42, -2.54) * mm});
            skLineSegment(sketch, "E55.top", {"start": v(-2.54, -33.02) * mm, "end": v(-58.42, -33.02) * mm});
            skLineSegment(sketch, "E55.left", {"start": v(-2.54, -2.54) * mm, "end": v(-2.54, -33.02) * mm});
            skLineSegment(sketch, "E55.right", {"start": v(-58.42, -2.54) * mm, "end": v(-58.42, -33.02) * mm});
            skLineSegment(sketch, "E56.bottom", {"start": v(58.42, -33.02) * mm, "end": v(2.54, -33.02) * mm});
            skLineSegment(sketch, "E56.top", {"start": v(58.42, -2.54) * mm, "end": v(2.54, -2.54) * mm});
            skLineSegment(sketch, "E56.left", {"start": v(58.42, -33.02) * mm, "end": v(58.42, -2.54) * mm});
            skLineSegment(sketch, "E56.right", {"start": v(2.54, -33.02) * mm, "end": v(2.54, -2.54) * mm});
            skSolve(sketch);
        }
        {
            var Q0;
            {var subQ0=sQuery(id+"F10.wireOp",EDGE,"E42");var subQ1=sQuery(id+"F10.wireOp",EDGE,"E41");var subQ2=makeQuery(id+"F10.imprint","INTERSECT",VERTEX,{"derivedFrom":[subQ1,subQ0]});Q0=makeQuery(id+"F10.imprint","IMPRINT",FACE,{"disambiguationData":[TD([[makeQuery(id+"F10.imprint","IMPRINT",EDGE,{"disambiguationData":[TD([[subQ2,-1.0]])],"derivedFrom":subQ1}),1.0]])]});}
            var Q1;
            {var subQ0=sQuery(id+"F10.wireOp",EDGE,"E42");var subQ1=sQuery(id+"F10.wireOp",EDGE,"E41");var subQ2=makeQuery(id+"F10.imprint","INTERSECT",VERTEX,{"derivedFrom":[subQ1,subQ0]});Q1=makeQuery(id+"F10.imprint","IMPRINT",FACE,{"disambiguationData":[TD([[makeQuery(id+"F10.imprint","IMPRINT",EDGE,{"disambiguationData":[TD([[subQ2,-1.0]])],"derivedFrom":subQ1}),-1.0]])]});}
            var Q2;
            {var subQ0=sQuery(id+"F10.wireOp",EDGE,"E53.top");var subQ1=sQuery(id+"F10.wireOp",EDGE,"E41");var subQ2=makeQuery(id+"F10.imprint","INTERSECT",VERTEX,{"derivedFrom":[subQ1,subQ0]});Q2=makeQuery(id+"F10.imprint","IMPRINT",FACE,{"disambiguationData":[TD([[makeQuery(id+"F10.imprint","IMPRINT",EDGE,{"disambiguationData":[TD([[subQ2,-1.0]])],"derivedFrom":subQ1}),-1.0]])]});}
            var Q3;
            {var subQ0=sQuery(id+"F10.wireOp",EDGE,"E53.top");var subQ1=sQuery(id+"F10.wireOp",EDGE,"E41");var subQ2=makeQuery(id+"F10.imprint","INTERSECT",VERTEX,{"derivedFrom":[subQ1,subQ0]});Q3=makeQuery(id+"F10.imprint","IMPRINT",FACE,{"disambiguationData":[TD([[makeQuery(id+"F10.imprint","IMPRINT",EDGE,{"disambiguationData":[TD([[subQ2,-1.0]])],"derivedFrom":subQ1}),1.0]])]});}
            var Q4;
            {var subQ0=sQuery(id+"F10.wireOp",EDGE,"E54.right");var subQ1=sQuery(id+"F10.wireOp",EDGE,"E43");var subQ2=makeQuery(id+"F10.imprint","INTERSECT",VERTEX,{"derivedFrom":[subQ1,subQ0]});Q4=makeQuery(id+"F10.imprint","IMPRINT",FACE,{"disambiguationData":[TD([[makeQuery(id+"F10.imprint","IMPRINT",EDGE,{"disambiguationData":[TD([[subQ2,-1.0]])],"derivedFrom":subQ1}),1.0]])]});}
            var Q5;
            {var subQ0=sQuery(id+"F10.wireOp",EDGE,"E54.right");var subQ1=sQuery(id+"F10.wireOp",EDGE,"E43");var subQ2=makeQuery(id+"F10.imprint","INTERSECT",VERTEX,{"derivedFrom":[subQ1,subQ0]});Q5=makeQuery(id+"F10.imprint","IMPRINT",FACE,{"disambiguationData":[TD([[makeQuery(id+"F10.imprint","IMPRINT",EDGE,{"disambiguationData":[TD([[subQ2,-1.0]])],"derivedFrom":subQ1}),-1.0]])]});}
            var Q6;
            {var subQ0=sQuery(id+"F10.wireOp",EDGE,"E44");var subQ1=sQuery(id+"F10.wireOp",EDGE,"E43");var subQ2=makeQuery(id+"F10.imprint","INTERSECT",VERTEX,{"derivedFrom":[subQ1,subQ0]});Q6=makeQuery(id+"F10.imprint","IMPRINT",FACE,{"disambiguationData":[TD([[makeQuery(id+"F10.imprint","IMPRINT",EDGE,{"disambiguationData":[TD([[subQ2,-1.0]])],"derivedFrom":subQ1}),1.0]])]});}
            var Q7;
            {var subQ0=sQuery(id+"F10.wireOp",EDGE,"E44");var subQ1=sQuery(id+"F10.wireOp",EDGE,"E43");var subQ2=makeQuery(id+"F10.imprint","INTERSECT",VERTEX,{"derivedFrom":[subQ1,subQ0]});Q7=makeQuery(id+"F10.imprint","IMPRINT",FACE,{"disambiguationData":[TD([[makeQuery(id+"F10.imprint","IMPRINT",EDGE,{"disambiguationData":[TD([[subQ2,-1.0]])],"derivedFrom":subQ1}),-1.0]])]});}
            var Q8;
            {var subQ0=sQuery(id+"F10.wireOp",EDGE,"E47");var subQ1=sQuery(id+"F10.wireOp",EDGE,"E46");var subQ2=makeQuery(id+"F10.imprint","INTERSECT",VERTEX,{"derivedFrom":[subQ1,subQ0]});Q8=makeQuery(id+"F10.imprint","IMPRINT",FACE,{"disambiguationData":[TD([[makeQuery(id+"F10.imprint","IMPRINT",EDGE,{"disambiguationData":[TD([[subQ2,-1.0]])],"derivedFrom":subQ1}),1.0]])]});}
            var Q9;
            {var subQ0=sQuery(id+"F10.wireOp",EDGE,"E47");var subQ1=sQuery(id+"F10.wireOp",EDGE,"E46");var subQ2=makeQuery(id+"F10.imprint","INTERSECT",VERTEX,{"derivedFrom":[subQ1,subQ0]});Q9=makeQuery(id+"F10.imprint","IMPRINT",FACE,{"disambiguationData":[TD([[makeQuery(id+"F10.imprint","IMPRINT",EDGE,{"disambiguationData":[TD([[subQ2,-1.0]])],"derivedFrom":subQ1}),-1.0]])]});}
            var Q10;
            {var subQ0=sQuery(id+"F10.wireOp",EDGE,"E55.top");var subQ1=sQuery(id+"F10.wireOp",EDGE,"E46");var subQ2=makeQuery(id+"F10.imprint","INTERSECT",VERTEX,{"derivedFrom":[subQ1,subQ0]});Q10=makeQuery(id+"F10.imprint","IMPRINT",FACE,{"disambiguationData":[TD([[makeQuery(id+"F10.imprint","IMPRINT",EDGE,{"disambiguationData":[TD([[subQ2,-1.0]])],"derivedFrom":subQ1}),-1.0]])]});}
            var Q11;
            {var subQ0=sQuery(id+"F10.wireOp",EDGE,"E55.top");var subQ1=sQuery(id+"F10.wireOp",EDGE,"E46");var subQ2=makeQuery(id+"F10.imprint","INTERSECT",VERTEX,{"derivedFrom":[subQ1,subQ0]});Q11=makeQuery(id+"F10.imprint","IMPRINT",FACE,{"disambiguationData":[TD([[makeQuery(id+"F10.imprint","IMPRINT",EDGE,{"disambiguationData":[TD([[subQ2,-1.0]])],"derivedFrom":subQ1}),1.0]])]});}
            var Q12;
            {var subQ0=sQuery(id+"F10.wireOp",EDGE,"E48");var subQ1=sQuery(id+"F10.wireOp",EDGE,"E45");var subQ2=makeQuery(id+"F10.imprint","INTERSECT",VERTEX,{"derivedFrom":[subQ1,subQ0]});Q12=makeQuery(id+"F10.imprint","IMPRINT",FACE,{"disambiguationData":[TD([[makeQuery(id+"F10.imprint","IMPRINT",EDGE,{"disambiguationData":[TD([[subQ2,-1.0]])],"derivedFrom":subQ1}),-1.0]])]});}
            var Q13;
            {var subQ0=sQuery(id+"F10.wireOp",EDGE,"E56.top");var subQ1=sQuery(id+"F10.wireOp",EDGE,"E45");var subQ2=makeQuery(id+"F10.imprint","INTERSECT",VERTEX,{"derivedFrom":[subQ1,subQ0]});Q13=makeQuery(id+"F10.imprint","IMPRINT",FACE,{"disambiguationData":[TD([[makeQuery(id+"F10.imprint","IMPRINT",EDGE,{"disambiguationData":[TD([[subQ2,-1.0]])],"derivedFrom":subQ1}),-1.0]])]});}
            var Q14;
            {var subQ0=sQuery(id+"F10.wireOp",EDGE,"E48");var subQ1=sQuery(id+"F10.wireOp",EDGE,"E45");var subQ2=makeQuery(id+"F10.imprint","INTERSECT",VERTEX,{"derivedFrom":[subQ1,subQ0]});Q14=makeQuery(id+"F10.imprint","IMPRINT",FACE,{"disambiguationData":[TD([[makeQuery(id+"F10.imprint","IMPRINT",EDGE,{"disambiguationData":[TD([[subQ2,-1.0]])],"derivedFrom":subQ1}),1.0]])]});}
            var Q15;
            {var subQ0=sQuery(id+"F10.wireOp",EDGE,"E56.top");var subQ1=sQuery(id+"F10.wireOp",EDGE,"E45");var subQ2=makeQuery(id+"F10.imprint","INTERSECT",VERTEX,{"derivedFrom":[subQ1,subQ0]});Q15=makeQuery(id+"F10.imprint","IMPRINT",FACE,{"disambiguationData":[TD([[makeQuery(id+"F10.imprint","IMPRINT",EDGE,{"disambiguationData":[TD([[subQ2,-1.0]])],"derivedFrom":subQ1}),1.0]])]});}
            var Q16;
            Q16=makeQuery(id+"F9.boolean.opBoolean","MERGE",FACE,{"derivedFrom":[makeQuery(id+"F7.boolean.opBoolean","COPY",FACE,{"derivedFrom":makeQuery(id+"F7.opExtrude","SWEPT_FACE",FACE,{"disambiguationData":[OSD([sQuery(id+"F6.wireOp",EDGE,"E22.top")])]})}),makeQuery(id+"F7.boolean.opBoolean","COPY",FACE,{"derivedFrom":makeQuery(id+"F7.opExtrude","SWEPT_FACE",FACE,{"disambiguationData":[OSD([sQuery(id+"F6.wireOp",EDGE,"E23.top")])]})}),makeQuery(id+"F9.opExtrude","SWEPT_FACE",FACE,{"disambiguationData":[OSD([sQuery(id+"F8.wireOp",EDGE,"E34.top")])]}),makeQuery(id+"F9.opExtrude","SWEPT_FACE",FACE,{"disambiguationData":[OSD([sQuery(id+"F8.wireOp",EDGE,"E35.top")])]})]});
            extrude(context, id + "F11", {"entities" : qUnion([Q0, Q1, Q2, Q3, Q4, Q5, Q6, Q7, Q8, Q9, Q10, Q11, Q12, Q13, Q14, Q15]), "operationType" : NewBodyOperationType.REMOVE, "endBound" : BoundingType.UP_TO_SURFACE, "oppositeDirection" : true, "endBoundEntityFace" : qUnion([Q16]), "depth" : 25.4 * mm});
        }
        {
            var Q0;
            {var subQ0=sQuery(id+"F2.wireOp",EDGE,"E1.right");var subQ1=sQuery(id+"F2.wireOp",EDGE,"E1.top");var subQ2=makeQuery(id+"F2.imprint","INTERSECT",VERTEX,{"derivedFrom":[subQ1,subQ0]});Q0=makeQuery(id+"F2.imprint","IMPRINT",FACE,{"disambiguationData":[TD([[makeQuery(id+"F2.imprint","IMPRINT",EDGE,{"disambiguationData":[TD([[subQ2,1.0]])],"derivedFrom":subQ1}),1.0]])]});}
            var Q1;
            {var subQ0=sQuery(id+"F2.wireOp",EDGE,"E8.top");Q1=makeQuery(id+"F2.imprint","IMPRINT",FACE,{"disambiguationData":[TD([[makeQuery(id+"F2.imprint","IMPRINT",EDGE,{"derivedFrom":subQ0}),-1.0]])]});}
            var Q2;
            {var subQ0=sQuery(id+"F2.wireOp",EDGE,"E1.right");var subQ1=sQuery(id+"F2.wireOp",EDGE,"E1.bottom");var subQ2=makeQuery(id+"F2.imprint","INTERSECT",VERTEX,{"derivedFrom":[subQ1,subQ0]});Q2=makeQuery(id+"F2.imprint","IMPRINT",FACE,{"disambiguationData":[TD([[makeQuery(id+"F2.imprint","IMPRINT",EDGE,{"disambiguationData":[TD([[subQ2,1.0]])],"derivedFrom":subQ1}),-1.0]])]});}
            var Q3;
            {var subQ4=sQuery(id+"F2.wireOp",EDGE,"E9.bottom");Q3=makeQuery(id+"F2.imprint","IMPRINT",FACE,{"disambiguationData":[TD([[makeQuery(id+"F2.imprint","IMPRINT",EDGE,{"derivedFrom":subQ4}),1.0]])]});}
            var Q4;
            {var subQ8=sQuery(id+"F2.wireOp",EDGE,"E7.bottom");Q4=makeQuery(id+"F2.imprint","IMPRINT",FACE,{"disambiguationData":[TD([[makeQuery(id+"F2.imprint","IMPRINT",EDGE,{"derivedFrom":subQ8}),1.0]])]});}
            var Q5;
            {var subQ0=sQuery(id+"F2.wireOp",EDGE,"E1.left");var subQ1=sQuery(id+"F2.wireOp",EDGE,"E1.bottom");var subQ2=makeQuery(id+"F2.imprint","INTERSECT",VERTEX,{"derivedFrom":[subQ1,subQ0]});Q5=makeQuery(id+"F2.imprint","IMPRINT",FACE,{"disambiguationData":[TD([[makeQuery(id+"F2.imprint","IMPRINT",EDGE,{"disambiguationData":[TD([[subQ2,-1.0]])],"derivedFrom":subQ1}),-1.0]])]});}
            var Q6;
            {var subQ0=sQuery(id+"F2.wireOp",EDGE,"E6.top");Q6=makeQuery(id+"F2.imprint","IMPRINT",FACE,{"disambiguationData":[TD([[makeQuery(id+"F2.imprint","IMPRINT",EDGE,{"derivedFrom":subQ0}),-1.0]])]});}
            var Q7;
            {var subQ0=sQuery(id+"F2.wireOp",EDGE,"E1.left");var subQ1=sQuery(id+"F2.wireOp",EDGE,"E1.top");var subQ2=makeQuery(id+"F2.imprint","INTERSECT",VERTEX,{"derivedFrom":[subQ1,subQ0]});Q7=makeQuery(id+"F2.imprint","IMPRINT",FACE,{"disambiguationData":[TD([[makeQuery(id+"F2.imprint","IMPRINT",EDGE,{"disambiguationData":[TD([[subQ2,-1.0]])],"derivedFrom":subQ1}),1.0]])]});}
            extrude(context, id + "F12", {"entities" : qUnion([Q0, Q1, Q2, Q3, Q4, Q5, Q6, Q7]), "operationType" : NewBodyOperationType.REMOVE, "endBound" : BoundingType.THROUGH_ALL, "depth" : 25.4 * mm});
        }
        {
            var Q0;
            Q0=makeQuery(id+"F1.opExtrude","CAP_FACE",FACE,{"disambiguationData":[OSD([sQuery(id+"F0.wireOp",EDGE,"E0.bottom"),sQuery(id+"F0.wireOp",EDGE,"E0.top"),sQuery(id+"F0.wireOp",EDGE,"E0.left"),sQuery(id+"F0.wireOp",EDGE,"E0.right")])],"isStart":true});
            var sketch = newSketch(context, id + "F13", { "sketchPlane" : qUnion([Q0])});
            skLineSegment(sketch, "E57", {"start": v(0, 23.81) * mm, "end": v(0, 35.56) * mm});
            skLineSegment(sketch, "E58", {"start": v(0, -23.81) * mm, "end": v(0, -35.56) * mm});
            skLineSegment(sketch, "E59.bottom", {"start": v(-42.55, 26.35) * mm, "end": v(42.55, 26.35) * mm});
            skLineSegment(sketch, "E59.top", {"start": v(-42.55, 33.02) * mm, "end": v(42.55, 33.02) * mm});
            skLineSegment(sketch, "E59.left", {"start": v(-42.55, 26.35) * mm, "end": v(-42.55, 33.02) * mm});
            skLineSegment(sketch, "E59.right", {"start": v(42.55, 26.35) * mm, "end": v(42.55, 33.02) * mm});
            skPoint(sketch, "E59.middle", {"position": v(0, 29.69) * mm});
            skLineSegment(sketch, "E60.bottom", {"start": v(2.54, 26.35) * mm, "end": v(-2.54, 26.35) * mm});
            skLineSegment(sketch, "E60.top", {"start": v(2.54, 33.02) * mm, "end": v(-2.54, 33.02) * mm});
            skLineSegment(sketch, "E60.left", {"start": v(2.54, 26.35) * mm, "end": v(2.54, 33.02) * mm});
            skLineSegment(sketch, "E60.right", {"start": v(-2.54, 26.35) * mm, "end": v(-2.54, 33.02) * mm});
            skLineSegment(sketch, "E61.bottom", {"start": v(-42.55, -33.02) * mm, "end": v(42.55, -33.02) * mm});
            skLineSegment(sketch, "E61.top", {"start": v(-42.55, -26.35) * mm, "end": v(42.55, -26.35) * mm});
            skLineSegment(sketch, "E61.left", {"start": v(-42.55, -33.02) * mm, "end": v(-42.55, -26.35) * mm});
            skLineSegment(sketch, "E61.right", {"start": v(42.55, -33.02) * mm, "end": v(42.55, -26.35) * mm});
            skPoint(sketch, "E61.middle", {"position": v(0, -29.69) * mm});
            skLineSegment(sketch, "E62.bottom", {"start": v(2.54, -33.02) * mm, "end": v(-2.54, -33.02) * mm});
            skLineSegment(sketch, "E62.top", {"start": v(2.54, -26.35) * mm, "end": v(-2.54, -26.35) * mm});
            skLineSegment(sketch, "E62.left", {"start": v(2.54, -33.02) * mm, "end": v(2.54, -26.35) * mm});
            skLineSegment(sketch, "E62.right", {"start": v(-2.54, -33.02) * mm, "end": v(-2.54, -26.35) * mm});
            skSolve(sketch);
        }
        {
            var Q0;
            {var subQ0=sQuery(id+"F13.wireOp",EDGE,"E59.right");Q0=makeQuery(id+"F13.imprint","IMPRINT",FACE,{"disambiguationData":[TD([[makeQuery(id+"F13.imprint","IMPRINT",EDGE,{"derivedFrom":subQ0}),1.0]])]});}
            var Q1;
            {var subQ0=sQuery(id+"F13.wireOp",EDGE,"E59.left");Q1=makeQuery(id+"F13.imprint","IMPRINT",FACE,{"disambiguationData":[TD([[makeQuery(id+"F13.imprint","IMPRINT",EDGE,{"derivedFrom":subQ0}),-1.0]])]});}
            var Q2;
            {var subQ0=sQuery(id+"F13.wireOp",EDGE,"E61.right");Q2=makeQuery(id+"F13.imprint","IMPRINT",FACE,{"disambiguationData":[TD([[makeQuery(id+"F13.imprint","IMPRINT",EDGE,{"derivedFrom":subQ0}),1.0]])]});}
            var Q3;
            {var subQ0=sQuery(id+"F13.wireOp",EDGE,"E61.left");Q3=makeQuery(id+"F13.imprint","IMPRINT",FACE,{"disambiguationData":[TD([[makeQuery(id+"F13.imprint","IMPRINT",EDGE,{"derivedFrom":subQ0}),-1.0]])]});}
            extrude(context, id + "F14", {"entities" : qUnion([Q0, Q1, Q2, Q3]), "operationType" : NewBodyOperationType.REMOVE, "endBound" : BoundingType.THROUGH_ALL, "oppositeDirection" : true, "depth" : 25.4 * mm});
        }
        {
            var Q0;
            Q0=makeQuery(id+"F1.opExtrude","SWEPT_FACE",FACE,{"disambiguationData":[OSD([sQuery(id+"F0.wireOp",EDGE,"E0.top")])]});
            var sketch = newSketch(context, id + "F15", { "sketchPlane" : qUnion([Q0])});
            skLineSegment(sketch, "E63", {"start": v(0, 20.32) * mm, "end": v(0, 0) * mm});
            skLineSegment(sketch, "E64.bottom", {"start": v(-42.55, 17.78) * mm, "end": v(42.55, 17.78) * mm});
            skLineSegment(sketch, "E64.top", {"start": v(-42.55, 2.54) * mm, "end": v(42.55, 2.54) * mm});
            skLineSegment(sketch, "E64.left", {"start": v(-42.55, 17.78) * mm, "end": v(-42.55, 2.54) * mm});
            skLineSegment(sketch, "E64.right", {"start": v(42.55, 17.78) * mm, "end": v(42.55, 2.54) * mm});
            skPoint(sketch, "E64.middle", {"position": v(0, 10.16) * mm});
            skLineSegment(sketch, "E65.bottom", {"start": v(-2.54, 17.78) * mm, "end": v(2.54, 17.78) * mm});
            skLineSegment(sketch, "E65.top", {"start": v(-2.54, 2.54) * mm, "end": v(2.54, 2.54) * mm});
            skLineSegment(sketch, "E65.left", {"start": v(-2.54, 17.78) * mm, "end": v(-2.54, 2.54) * mm});
            skLineSegment(sketch, "E65.right", {"start": v(2.54, 17.78) * mm, "end": v(2.54, 2.54) * mm});
            skSolve(sketch);
        }
        {
            var Q0;
            {var subQ0=sQuery(id+"F15.wireOp",EDGE,"E64.right");Q0=makeQuery(id+"F15.imprint","IMPRINT",FACE,{"disambiguationData":[TD([[makeQuery(id+"F15.imprint","IMPRINT",EDGE,{"derivedFrom":subQ0}),-1.0]])]});}
            var Q1;
            {var subQ0=sQuery(id+"F15.wireOp",EDGE,"E64.left");Q1=makeQuery(id+"F15.imprint","IMPRINT",FACE,{"disambiguationData":[TD([[makeQuery(id+"F15.imprint","IMPRINT",EDGE,{"derivedFrom":subQ0}),1.0]])]});}
            extrude(context, id + "F16", {"entities" : qUnion([Q0, Q1]), "operationType" : NewBodyOperationType.REMOVE, "oppositeDirection" : true, "depth" : 4.27 * mm});
        }
        {
            var Q0;
            Q0=makeQuery(id+"F1.opExtrude","SWEPT_FACE",FACE,{"disambiguationData":[OSD([sQuery(id+"F0.wireOp",EDGE,"E0.bottom")])]});
            var sketch = newSketch(context, id + "F17", { "sketchPlane" : qUnion([Q0])});
            skLineSegment(sketch, "E66", {"start": v(0, 20.32) * mm, "end": v(0, 0) * mm});
            skLineSegment(sketch, "E67.bottom", {"start": v(-42.55, 2.54) * mm, "end": v(42.55, 2.54) * mm});
            skLineSegment(sketch, "E67.top", {"start": v(-42.55, 17.78) * mm, "end": v(42.55, 17.78) * mm});
            skLineSegment(sketch, "E67.left", {"start": v(-42.55, 2.54) * mm, "end": v(-42.55, 17.78) * mm});
            skLineSegment(sketch, "E67.right", {"start": v(42.55, 2.54) * mm, "end": v(42.55, 17.78) * mm});
            skPoint(sketch, "E67.middle", {"position": v(0, 10.16) * mm});
            skLineSegment(sketch, "E68.bottom", {"start": v(2.54, 2.54) * mm, "end": v(-2.54, 2.54) * mm});
            skLineSegment(sketch, "E68.top", {"start": v(2.54, 17.78) * mm, "end": v(-2.54, 17.78) * mm});
            skLineSegment(sketch, "E68.left", {"start": v(2.54, 2.54) * mm, "end": v(2.54, 17.78) * mm});
            skLineSegment(sketch, "E68.right", {"start": v(-2.54, 2.54) * mm, "end": v(-2.54, 17.78) * mm});
            skSolve(sketch);
        }
        {
            var Q0;
            {var subQ0=sQuery(id+"F17.wireOp",EDGE,"E67.right");Q0=makeQuery(id+"F17.imprint","IMPRINT",FACE,{"disambiguationData":[TD([[makeQuery(id+"F17.imprint","IMPRINT",EDGE,{"derivedFrom":subQ0}),1.0]])]});}
            var Q1;
            {var subQ0=sQuery(id+"F17.wireOp",EDGE,"E67.left");Q1=makeQuery(id+"F17.imprint","IMPRINT",FACE,{"disambiguationData":[TD([[makeQuery(id+"F17.imprint","IMPRINT",EDGE,{"derivedFrom":subQ0}),-1.0]])]});}
            extrude(context, id + "F18", {"entities" : qUnion([Q0, Q1]), "operationType" : NewBodyOperationType.REMOVE, "oppositeDirection" : true, "depth" : 4.03 * mm});
        }
        {
            var Q0;
            Q0=makeQuery(id+"F1.opExtrude","CAP_FACE",FACE,{"disambiguationData":[OSD([sQuery(id+"F0.wireOp",EDGE,"E0.bottom"),sQuery(id+"F0.wireOp",EDGE,"E0.top"),sQuery(id+"F0.wireOp",EDGE,"E0.left"),sQuery(id+"F0.wireOp",EDGE,"E0.right")])],"isStart":true});
            var sketch = newSketch(context, id + "F19", { "sketchPlane" : qUnion([Q0])});
            skLineSegment(sketch, "E69", {"start": v(60.96, 0) * mm, "end": v(34.93, 0) * mm});
            skLineSegment(sketch, "E70", {"start": v(-34.93, 0) * mm, "end": v(-60.96, 0) * mm});
            skLineSegment(sketch, "E71.bottom", {"start": v(-37.46, -17.15) * mm, "end": v(-58.42, -17.15) * mm});
            skLineSegment(sketch, "E71.top", {"start": v(-37.46, 17.15) * mm, "end": v(-58.42, 17.15) * mm});
            skLineSegment(sketch, "E71.left", {"start": v(-37.46, -17.15) * mm, "end": v(-37.46, 17.15) * mm});
            skLineSegment(sketch, "E71.right", {"start": v(-58.42, -17.15) * mm, "end": v(-58.42, 17.15) * mm});
            skPoint(sketch, "E71.middle", {"position": v(-47.94, 0) * mm});
            skLineSegment(sketch, "E72.bottom", {"start": v(37.46, -17.14) * mm, "end": v(58.42, -17.14) * mm});
            skLineSegment(sketch, "E72.top", {"start": v(37.46, 17.14) * mm, "end": v(58.42, 17.14) * mm});
            skLineSegment(sketch, "E72.left", {"start": v(37.46, -17.14) * mm, "end": v(37.46, 17.14) * mm});
            skLineSegment(sketch, "E72.right", {"start": v(58.42, -17.14) * mm, "end": v(58.42, 17.14) * mm});
            skPoint(sketch, "E72.middle", {"position": v(47.94, 0) * mm});
            skLineSegment(sketch, "E73.bottom", {"start": v(-37.46, -2.54) * mm, "end": v(-58.42, -2.54) * mm});
            skLineSegment(sketch, "E73.top", {"start": v(-37.46, 2.54) * mm, "end": v(-58.42, 2.54) * mm});
            skLineSegment(sketch, "E73.left", {"start": v(-37.46, -2.54) * mm, "end": v(-37.46, 2.54) * mm});
            skLineSegment(sketch, "E73.right", {"start": v(-58.42, -2.54) * mm, "end": v(-58.42, 2.54) * mm});
            skLineSegment(sketch, "E74.bottom", {"start": v(37.46, 2.54) * mm, "end": v(58.42, 2.54) * mm});
            skLineSegment(sketch, "E74.top", {"start": v(37.46, -2.54) * mm, "end": v(58.42, -2.54) * mm});
            skLineSegment(sketch, "E74.left", {"start": v(37.46, 2.54) * mm, "end": v(37.46, -2.54) * mm});
            skLineSegment(sketch, "E74.right", {"start": v(58.42, 2.54) * mm, "end": v(58.42, -2.54) * mm});
            skSolve(sketch);
        }
        {
            var Q0;
            {var subQ0=sQuery(id+"F19.wireOp",EDGE,"E72.top");Q0=makeQuery(id+"F19.imprint","IMPRINT",FACE,{"disambiguationData":[TD([[makeQuery(id+"F19.imprint","IMPRINT",EDGE,{"derivedFrom":subQ0}),-1.0]])]});}
            var Q1;
            {var subQ0=sQuery(id+"F19.wireOp",EDGE,"E71.bottom");Q1=makeQuery(id+"F19.imprint","IMPRINT",FACE,{"disambiguationData":[TD([[makeQuery(id+"F19.imprint","IMPRINT",EDGE,{"derivedFrom":subQ0}),-1.0]])]});}
            var Q2;
            {var subQ0=sQuery(id+"F19.wireOp",EDGE,"E72.bottom");Q2=makeQuery(id+"F19.imprint","IMPRINT",FACE,{"disambiguationData":[TD([[makeQuery(id+"F19.imprint","IMPRINT",EDGE,{"derivedFrom":subQ0}),1.0]])]});}
            var Q3;
            {var subQ0=sQuery(id+"F19.wireOp",EDGE,"E71.top");Q3=makeQuery(id+"F19.imprint","IMPRINT",FACE,{"disambiguationData":[TD([[makeQuery(id+"F19.imprint","IMPRINT",EDGE,{"derivedFrom":subQ0}),1.0]])]});}
            extrude(context, id + "F20", {"entities" : qUnion([Q0, Q1, Q2, Q3]), "operationType" : NewBodyOperationType.REMOVE, "oppositeDirection" : true, "depth" : 25.4 * mm});
        }
        {
            var Q0;
            Q0=makeQuery(id+"F1.opExtrude","SWEPT_FACE",FACE,{"disambiguationData":[OSD([sQuery(id+"F0.wireOp",EDGE,"E0.left")])]});
            var sketch = newSketch(context, id + "F21", { "sketchPlane" : qUnion([Q0])});
            skLineSegment(sketch, "E75", {"start": v(0, 20.32) * mm, "end": v(0, 0) * mm});
            skLineSegment(sketch, "E76.bottom", {"start": v(17.15, 17.78) * mm, "end": v(-17.15, 17.78) * mm});
            skLineSegment(sketch, "E76.top", {"start": v(17.15, 2.54) * mm, "end": v(-17.15, 2.54) * mm});
            skLineSegment(sketch, "E76.left", {"start": v(17.15, 17.78) * mm, "end": v(17.15, 2.54) * mm});
            skLineSegment(sketch, "E76.right", {"start": v(-17.15, 17.78) * mm, "end": v(-17.15, 2.54) * mm});
            skPoint(sketch, "E76.middle", {"position": v(0, 10.16) * mm});
            skLineSegment(sketch, "E77.bottom", {"start": v(-2.54, 17.78) * mm, "end": v(2.54, 17.78) * mm});
            skLineSegment(sketch, "E77.top", {"start": v(-2.54, 2.54) * mm, "end": v(2.54, 2.54) * mm});
            skLineSegment(sketch, "E77.left", {"start": v(-2.54, 17.78) * mm, "end": v(-2.54, 2.54) * mm});
            skLineSegment(sketch, "E77.right", {"start": v(2.54, 17.78) * mm, "end": v(2.54, 2.54) * mm});
            skSolve(sketch);
        }
        {
            var Q0;
            {var subQ0=sQuery(id+"F21.wireOp",EDGE,"E76.left");Q0=makeQuery(id+"F21.imprint","IMPRINT",FACE,{"disambiguationData":[TD([[makeQuery(id+"F21.imprint","IMPRINT",EDGE,{"derivedFrom":subQ0}),-1.0]])]});}
            var Q1;
            {var subQ0=sQuery(id+"F21.wireOp",EDGE,"E76.right");Q1=makeQuery(id+"F21.imprint","IMPRINT",FACE,{"disambiguationData":[TD([[makeQuery(id+"F21.imprint","IMPRINT",EDGE,{"derivedFrom":subQ0}),1.0]])]});}
            extrude(context, id + "F22", {"entities" : qUnion([Q0, Q1]), "operationType" : NewBodyOperationType.REMOVE, "oppositeDirection" : true, "depth" : 17.7 * mm});
        }
        {
            var Q0;
            Q0=makeQuery(id+"F1.opExtrude","SWEPT_FACE",FACE,{"disambiguationData":[OSD([sQuery(id+"F0.wireOp",EDGE,"E0.right")])]});
            var sketch = newSketch(context, id + "F23", { "sketchPlane" : qUnion([Q0])});
            skLineSegment(sketch, "E78", {"start": v(0, 20.32) * mm, "end": v(0, 0) * mm});
            skLineSegment(sketch, "E79.bottom", {"start": v(17.15, 17.78) * mm, "end": v(-17.14, 17.78) * mm});
            skLineSegment(sketch, "E79.top", {"start": v(17.15, 2.54) * mm, "end": v(-17.14, 2.54) * mm});
            skLineSegment(sketch, "E79.left", {"start": v(17.15, 17.78) * mm, "end": v(17.15, 2.54) * mm});
            skLineSegment(sketch, "E79.right", {"start": v(-17.14, 17.78) * mm, "end": v(-17.14, 2.54) * mm});
            skPoint(sketch, "E79.middle", {"position": v(0, 10.16) * mm});
            skLineSegment(sketch, "E80.bottom", {"start": v(2.54, 17.78) * mm, "end": v(-2.54, 17.78) * mm});
            skLineSegment(sketch, "E80.top", {"start": v(2.54, 2.54) * mm, "end": v(-2.54, 2.54) * mm});
            skLineSegment(sketch, "E80.left", {"start": v(2.54, 17.78) * mm, "end": v(2.54, 2.54) * mm});
            skLineSegment(sketch, "E80.right", {"start": v(-2.54, 17.78) * mm, "end": v(-2.54, 2.54) * mm});
            skSolve(sketch);
        }
        {
            var Q0;
            {var subQ0=sQuery(id+"F23.wireOp",EDGE,"E79.right");Q0=makeQuery(id+"F23.imprint","IMPRINT",FACE,{"disambiguationData":[TD([[makeQuery(id+"F23.imprint","IMPRINT",EDGE,{"derivedFrom":subQ0}),1.0]])]});}
            var Q1;
            {var subQ0=sQuery(id+"F23.wireOp",EDGE,"E79.left");Q1=makeQuery(id+"F23.imprint","IMPRINT",FACE,{"disambiguationData":[TD([[makeQuery(id+"F23.imprint","IMPRINT",EDGE,{"derivedFrom":subQ0}),-1.0]])]});}
            extrude(context, id + "F24", {"entities" : qUnion([Q0, Q1]), "operationType" : NewBodyOperationType.REMOVE, "oppositeDirection" : true, "depth" : 16.13 * mm});
        }
        {
            var Q0;
            Q0=makeQuery(id+"F24.boolean.opBoolean","MERGE",FACE,{"derivedFrom":[makeQuery(id+"F20.boolean.opBoolean","COPY",FACE,{"derivedFrom":makeQuery(id+"F20.opExtrude","SWEPT_FACE",FACE,{"disambiguationData":[OSD([sQuery(id+"F19.wireOp",EDGE,"E74.bottom")])]})}),makeQuery(id+"F24.opExtrude","SWEPT_FACE",FACE,{"disambiguationData":[OSD([sQuery(id+"F23.wireOp",EDGE,"E80.right")])]})]});
            var sketch = newSketch(context, id + "F25", { "sketchPlane" : qUnion([Q0])});
            skLineSegment(sketch, "E81.bottom", {"start": v(58.42, 2.54) * mm, "end": v(37.46, 2.54) * mm});
            skLineSegment(sketch, "E81.top", {"start": v(58.42, 17.78) * mm, "end": v(37.46, 17.78) * mm});
            skLineSegment(sketch, "E81.left", {"start": v(58.42, 2.54) * mm, "end": v(58.42, 17.78) * mm});
            skLineSegment(sketch, "E81.right", {"start": v(37.46, 2.54) * mm, "end": v(37.46, 17.78) * mm});
            skSolve(sketch);
        }
        {
            var Q0;
            Q0=makeQuery(id+"F25.imprint","IMPRINT",FACE,{"disambiguationData":[TD([[makeQuery(id+"F25.imprint","IMPRINT",EDGE,{"derivedFrom":sQuery(id+"F25.wireOp",EDGE,"E81.bottom")}),-1.0]])]});
            extrude(context, id + "F26", {"entities" : qUnion([Q0]), "operationType" : NewBodyOperationType.REMOVE, "oppositeDirection" : true, "depth" : 12.7 * mm});
        }
        {
            var Q0;
            Q0=makeQuery(id+"F16.boolean.opBoolean","MERGE",FACE,{"derivedFrom":[makeQuery(id+"F14.boolean.opBoolean","COPY",FACE,{"derivedFrom":makeQuery(id+"F14.opExtrude","SWEPT_FACE",FACE,{"disambiguationData":[OSD([sQuery(id+"F13.wireOp",EDGE,"E60.left")])]})}),makeQuery(id+"F16.opExtrude","SWEPT_FACE",FACE,{"disambiguationData":[OSD([sQuery(id+"F15.wireOp",EDGE,"E65.right")])]})]});
            var sketch = newSketch(context, id + "F27", { "sketchPlane" : qUnion([Q0])});
            skLineSegment(sketch, "E82.bottom", {"start": v(-33.02, 2.54) * mm, "end": v(-26.35, 2.54) * mm});
            skLineSegment(sketch, "E82.top", {"start": v(-33.02, 17.78) * mm, "end": v(-26.35, 17.78) * mm});
            skLineSegment(sketch, "E82.left", {"start": v(-33.02, 2.54) * mm, "end": v(-33.02, 17.78) * mm});
            skLineSegment(sketch, "E82.right", {"start": v(-26.35, 2.54) * mm, "end": v(-26.35, 17.78) * mm});
            skSolve(sketch);
        }
        {
            var Q0;
            Q0=makeQuery(id+"F27.imprint","IMPRINT",FACE,{"disambiguationData":[TD([[makeQuery(id+"F27.imprint","IMPRINT",EDGE,{"derivedFrom":sQuery(id+"F27.wireOp",EDGE,"E82.bottom")}),1.0]])]});
            extrude(context, id + "F28", {"entities" : qUnion([Q0]), "operationType" : NewBodyOperationType.REMOVE, "oppositeDirection" : true, "depth" : 25.4 * mm});
        }
        {
            var Q0;
            Q0=makeQuery(id+"F18.boolean.opBoolean","MERGE",FACE,{"derivedFrom":[makeQuery(id+"F14.boolean.opBoolean","COPY",FACE,{"derivedFrom":makeQuery(id+"F14.opExtrude","SWEPT_FACE",FACE,{"disambiguationData":[OSD([sQuery(id+"F13.wireOp",EDGE,"E62.left")])]})}),makeQuery(id+"F18.opExtrude","SWEPT_FACE",FACE,{"disambiguationData":[OSD([sQuery(id+"F17.wireOp",EDGE,"E68.right")])]})]});
            var sketch = newSketch(context, id + "F29", { "sketchPlane" : qUnion([Q0])});
            skLineSegment(sketch, "E83.bottom", {"start": v(33.02, 2.54) * mm, "end": v(26.35, 2.54) * mm});
            skLineSegment(sketch, "E83.top", {"start": v(33.02, 17.78) * mm, "end": v(26.35, 17.78) * mm});
            skLineSegment(sketch, "E83.left", {"start": v(33.02, 2.54) * mm, "end": v(33.02, 17.78) * mm});
            skLineSegment(sketch, "E83.right", {"start": v(26.35, 2.54) * mm, "end": v(26.35, 17.78) * mm});
            skSolve(sketch);
        }
        {
            var Q0;
            Q0=makeQuery(id+"F29.imprint","IMPRINT",FACE,{"disambiguationData":[TD([[makeQuery(id+"F29.imprint","IMPRINT",EDGE,{"derivedFrom":sQuery(id+"F29.wireOp",EDGE,"E83.bottom")}),-1.0]])]});
            extrude(context, id + "F30", {"entities" : qUnion([Q0]), "operationType" : NewBodyOperationType.REMOVE, "oppositeDirection" : true, "depth" : 25.4 * mm});
        }
        {
            var Q0;
            Q0=makeQuery(id+"F22.boolean.opBoolean","MERGE",FACE,{"derivedFrom":[makeQuery(id+"F20.boolean.opBoolean","COPY",FACE,{"derivedFrom":makeQuery(id+"F20.opExtrude","SWEPT_FACE",FACE,{"disambiguationData":[OSD([sQuery(id+"F19.wireOp",EDGE,"E73.bottom")])]})}),makeQuery(id+"F22.opExtrude","SWEPT_FACE",FACE,{"disambiguationData":[OSD([sQuery(id+"F21.wireOp",EDGE,"E77.left")])]})]});
            var sketch = newSketch(context, id + "F31", { "sketchPlane" : qUnion([Q0])});
            skLineSegment(sketch, "E84.bottom", {"start": v(58.42, 2.54) * mm, "end": v(37.46, 2.54) * mm});
            skLineSegment(sketch, "E84.top", {"start": v(58.42, 17.78) * mm, "end": v(37.46, 17.78) * mm});
            skLineSegment(sketch, "E84.left", {"start": v(58.42, 2.54) * mm, "end": v(58.42, 17.78) * mm});
            skLineSegment(sketch, "E84.right", {"start": v(37.46, 2.54) * mm, "end": v(37.46, 17.78) * mm});
            skSolve(sketch);
        }
        {
            var Q0;
            Q0=makeQuery(id+"F31.imprint","IMPRINT",FACE,{"disambiguationData":[TD([[makeQuery(id+"F31.imprint","IMPRINT",EDGE,{"derivedFrom":sQuery(id+"F31.wireOp",EDGE,"E84.bottom")}),-1.0]])]});
            extrude(context, id + "F32", {"entities" : qUnion([Q0]), "operationType" : NewBodyOperationType.REMOVE, "oppositeDirection" : true, "depth" : 12.7 * mm});
        }
    });
